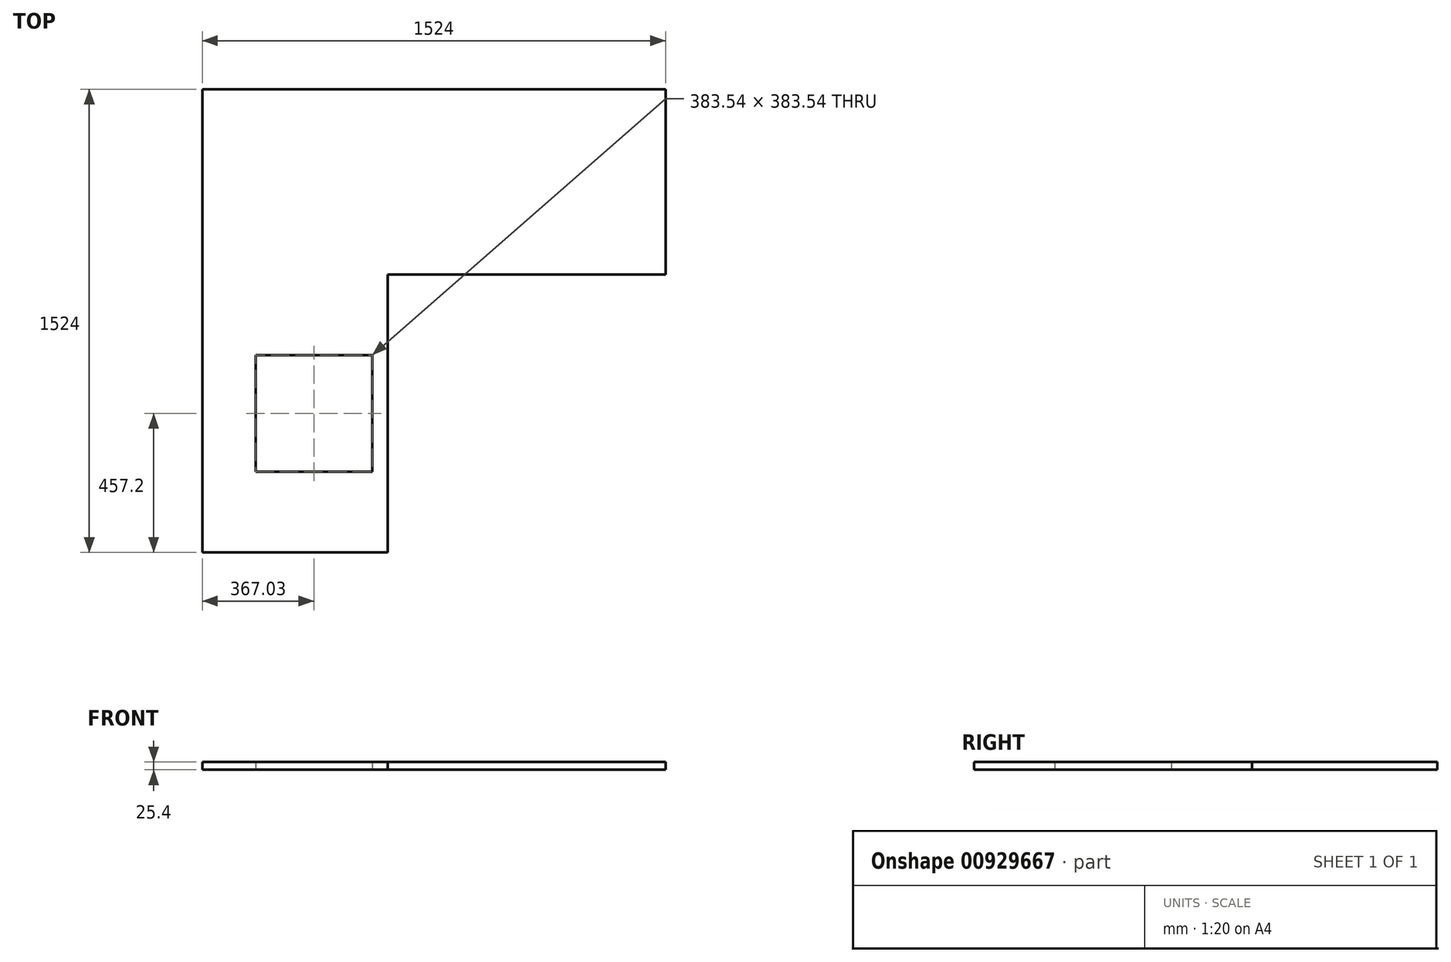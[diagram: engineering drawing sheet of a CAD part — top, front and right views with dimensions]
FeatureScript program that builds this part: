
annotation { "Feature Type Name" : "Feature", "Feature Type Description" : "" }
export const myFeature = defineFeature(function(context is Context, id is Id, definition is map)
    precondition{}
    {
        {
            var Q0;
            Q0=qCreatedBy(makeId("Top.planeOp"),FACE);
            var sketch = newSketch(context, id + "F0", { "sketchPlane" : qUnion([Q0])});
            skLineSegment(sketch, "E0.bottom", {"start": v(-434.34, -648.97) * mm, "end": v(-50.8, -648.97) * mm});
            skLineSegment(sketch, "E0.top", {"start": v(-434.34, -265.43) * mm, "end": v(-50.8, -265.43) * mm});
            skLineSegment(sketch, "E0.left", {"start": v(-434.34, -648.97) * mm, "end": v(-434.34, -265.43) * mm});
            skLineSegment(sketch, "E0.right", {"start": v(-50.8, -648.97) * mm, "end": v(-50.8, -265.43) * mm});
            skPoint(sketch, "E1", {"position": v(-278.78, -457.2) * mm});
            skSolve(sketch);
        }
        {
            var Q0;
            Q0=makeQuery(id+"F0.imprint","IMPRINT",FACE,{"disambiguationData":[TD([[makeQuery(id+"F0.imprint","IMPRINT",EDGE,{"derivedFrom":sQuery(id+"F0.wireOp",EDGE,"E0.bottom")}),1.0]])]});
            var sketch = newSketch(context, id + "F1", { "sketchPlane" : qUnion([Q0])});
            skLineSegment(sketch, "E2", {"start": v(0, 0) * mm, "end": v(914.4, 0) * mm});
            skLineSegment(sketch, "E3", {"start": v(914.4, 0) * mm, "end": v(914.4, 609.6) * mm});
            skLineSegment(sketch, "E4", {"start": v(914.4, 609.6) * mm, "end": v(-609.6, 609.6) * mm});
            skLineSegment(sketch, "E5", {"start": v(-609.6, 609.6) * mm, "end": v(-609.6, -914.4) * mm});
            skLineSegment(sketch, "E6", {"start": v(-609.6, -914.4) * mm, "end": v(0, -914.4) * mm});
            skLineSegment(sketch, "E7", {"start": v(0, -914.4) * mm, "end": v(0, 0) * mm});
            skSolve(sketch);
        }
        {
            var Q0;
            Q0=makeQuery(id+"F1.imprint","IMPRINT",FACE,{"disambiguationData":[TD([[makeQuery(id+"F1.imprint","IMPRINT",EDGE,{"derivedFrom":sQuery(id+"F1.wireOp",EDGE,"E2")}),1.0]])]});
            extrude(context, id + "F2", {"entities" : qUnion([Q0]), "depth" : 25.4 * mm, "offsetDistance" : 25.4 * mm});
        }
    });
